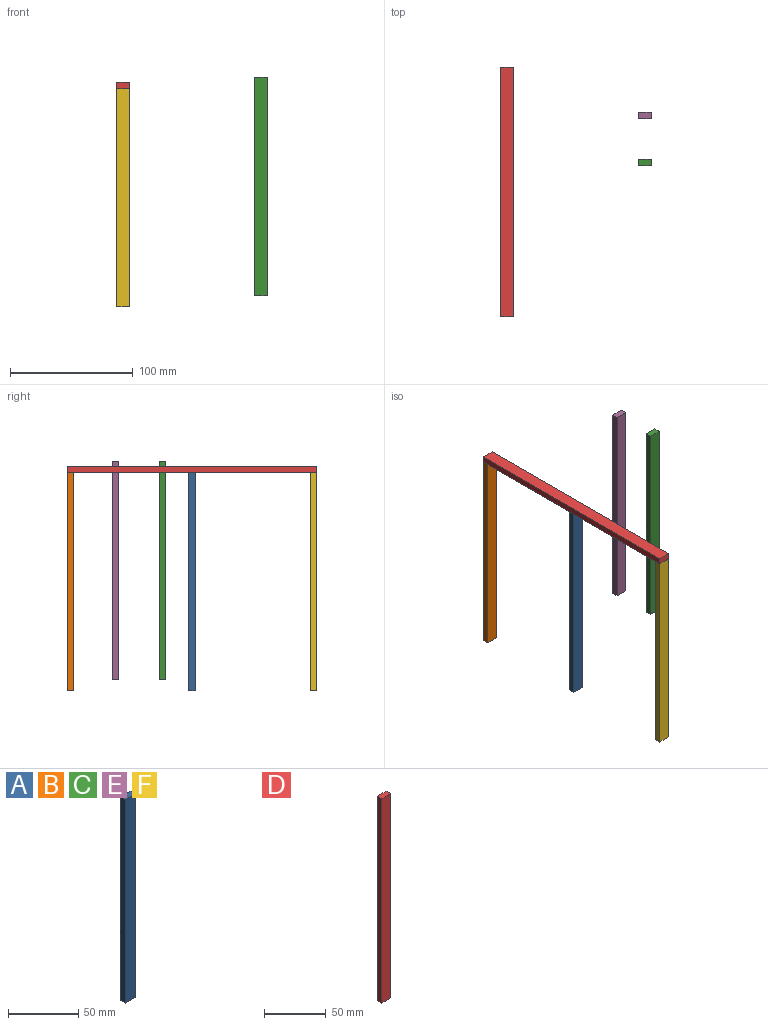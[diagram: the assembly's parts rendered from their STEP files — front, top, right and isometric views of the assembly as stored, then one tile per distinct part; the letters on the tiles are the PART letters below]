
ASSEMBLY  parts=6 mates=6
PART A: 6 faces, bbox 10.2x5.1x177.8 mm
  f0: plane 177.8x5.08mm, normal (-1,0,0), area 903.2mm2, adj f1,f3,f4,f5
  f1: plane 177.8x10.16mm, normal (0,-1,0), area 1806.4mm2, adj f0,f2,f4,f5
  f2: plane 177.8x5.08mm, normal (1,0,0), area 903.2mm2, adj f1,f3,f4,f5
  f3: plane 177.8x10.16mm, normal (0,1,0), area 1806.4mm2, adj f0,f2,f4,f5
  f4: plane 10.16x5.08mm, normal (0,0,1), area 51.6mm2, adj f0,f1,f2,f3
  f5: plane 10.16x5.08mm, normal (0,0,-1), area 51.6mm2, adj f0,f1,f2,f3
PART B: same geometry as A
PART C: same geometry as A
PART D: 6 faces, bbox 10.2x5.1x203.2 mm
  f0: plane 203.2x5.08mm, normal (-1,0,0), area 1032.3mm2, adj f1,f3,f4,f5
  f1: plane 203.2x10.16mm, normal (0,-1,0), area 2064.5mm2, adj f0,f2,f4,f5
  f2: plane 203.2x5.08mm, normal (1,0,0), area 1032.3mm2, adj f1,f3,f4,f5
  f3: plane 203.2x10.16mm, normal (0,1,0), area 2064.5mm2, adj f0,f2,f4,f5
  f4: plane 10.16x5.08mm, normal (0,0,1), area 51.6mm2, adj f0,f1,f2,f3
  f5: plane 10.16x5.08mm, normal (0,0,-1), area 51.6mm2, adj f0,f1,f2,f3
PART E: same geometry as A
PART F: same geometry as A
PLACE A t=(-112.33,-160.09,-20.67)mm
PLACE B t=(-112.33,-61.03,-20.67)mm
PLACE C t=(0,-136.13,-11.23)mm
PLACE D rot(axis=(-1,0,0),90deg) t=(-112.33,-160.09,70.77)mm
PLACE E t=(0,-97.62,-11.71)mm
PLACE F t=(-112.33,-259.1,-20.67)mm
MATE planar B.f4 <-> D.f3  axis (0,0,1) through (-112.33,-61.03,68.23)mm
MATE planar D.f2 <-> F.f2  axis (1,0,0) through (-107.25,-261.69,70.77)mm
MATE planar A.f4 <-> D.f3  axis (0,0,1) through (-112.33,-160.09,68.23)mm
MATE planar B.f2 <-> D.f2  axis (1,0,0) through (-107.25,-61.03,68.23)mm
MATE planar D.f4 <-> B.f3  axis (0,1,0) through (-112.33,-58.49,70.77)mm
MATE planar F.f4 <-> D.f3  axis (0,0,1) through (-112.33,-259.1,68.23)mm
